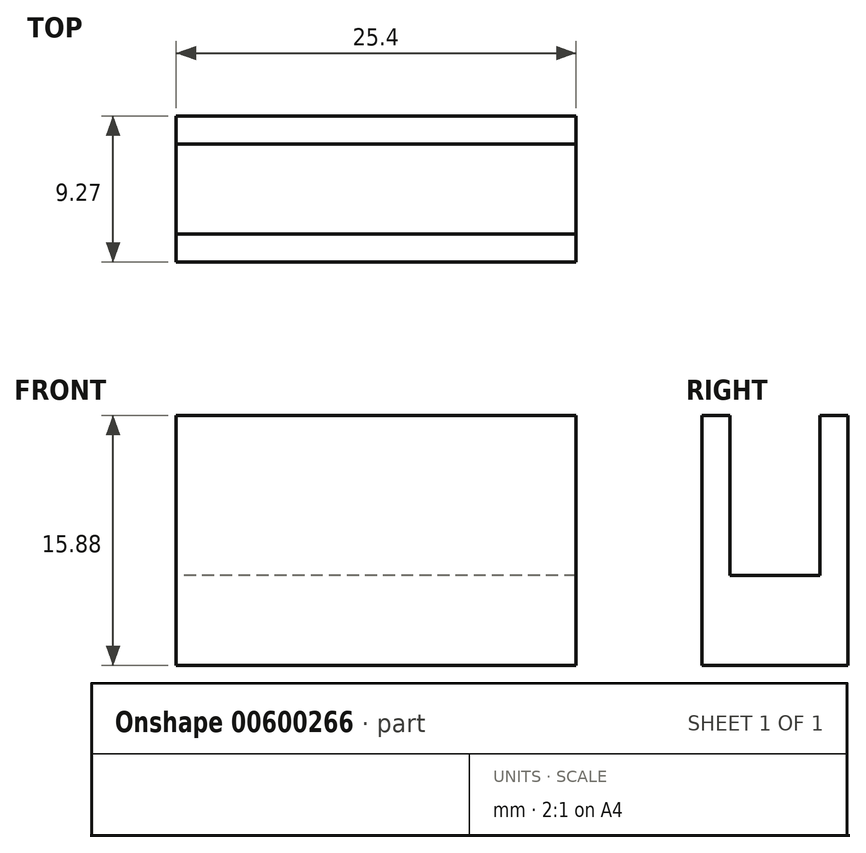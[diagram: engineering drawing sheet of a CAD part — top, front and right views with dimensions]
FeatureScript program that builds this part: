
annotation { "Feature Type Name" : "Feature", "Feature Type Description" : "" }
export const myFeature = defineFeature(function(context is Context, id is Id, definition is map)
    precondition{}
    {
        {
            var Q0;
            Q0=qCreatedBy(makeId("Top.planeOp"),FACE);
            var sketch = newSketch(context, id + "F0", { "sketchPlane" : qUnion([Q0])});
            skLineSegment(sketch, "E0.bottom", {"start": v(0, 0) * mm, "end": v(25.4, 0) * mm});
            skLineSegment(sketch, "E0.top", {"start": v(0, -9.27) * mm, "end": v(25.4, -9.27) * mm});
            skLineSegment(sketch, "E0.left", {"start": v(0, 0) * mm, "end": v(0, -9.27) * mm});
            skLineSegment(sketch, "E0.right", {"start": v(25.4, 0) * mm, "end": v(25.4, -9.27) * mm});
            skSolve(sketch);
        }
        {
            var Q0;
            Q0 = qSketchRegion(id + "F0", true);
            extrude(context, id + "F1", {"entities" : qUnion([Q0]), "depth" : 5.7 * mm, "offsetDistance" : 25.4 * mm});
        }
        {
            var Q0;
            Q0=makeQuery(id+"F1.opExtrude","CAP_FACE",FACE,{"disambiguationData":[OSD([sQuery(id+"F0.wireOp",EDGE,"E0.bottom"),sQuery(id+"F0.wireOp",EDGE,"E0.top"),sQuery(id+"F0.wireOp",EDGE,"E0.left"),sQuery(id+"F0.wireOp",EDGE,"E0.right")])],"isStart":false});
            var sketch = newSketch(context, id + "F2", { "sketchPlane" : qUnion([Q0])});
            skLineSegment(sketch, "E1.bottom", {"start": v(0, 0) * mm, "end": v(25.4, 0) * mm});
            skLineSegment(sketch, "E1.top", {"start": v(0, -1.78) * mm, "end": v(25.4, -1.78) * mm});
            skLineSegment(sketch, "E1.left", {"start": v(0, 0) * mm, "end": v(0, -1.78) * mm});
            skLineSegment(sketch, "E1.right", {"start": v(25.4, 0) * mm, "end": v(25.4, -1.78) * mm});
            skLineSegment(sketch, "E2.bottom", {"start": v(25.4, -9.27) * mm, "end": v(0, -9.27) * mm});
            skLineSegment(sketch, "E2.top", {"start": v(25.4, -7.5) * mm, "end": v(0, -7.5) * mm});
            skLineSegment(sketch, "E2.left", {"start": v(25.4, -9.27) * mm, "end": v(25.4, -7.5) * mm});
            skLineSegment(sketch, "E2.right", {"start": v(0, -9.27) * mm, "end": v(0, -7.5) * mm});
            skSolve(sketch);
        }
        {
            var Q0;
            Q0 = qSketchRegion(id + "F2", true);
            extrude(context, id + "F3", {"entities" : qUnion([Q0]), "operationType" : NewBodyOperationType.ADD, "depth" : 10.16 * mm, "offsetDistance" : 25.4 * mm});
        }
    });
